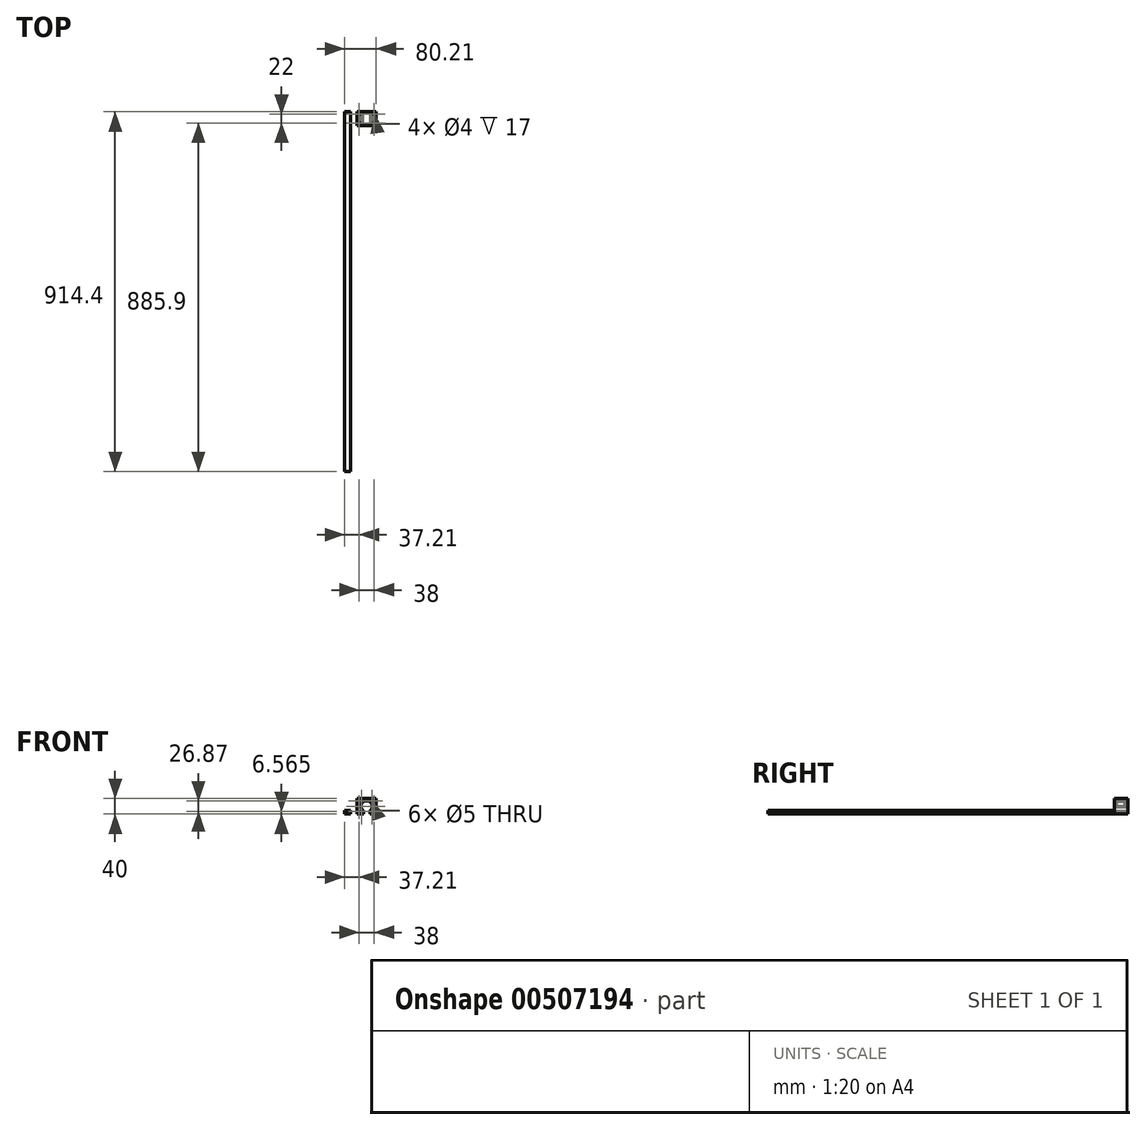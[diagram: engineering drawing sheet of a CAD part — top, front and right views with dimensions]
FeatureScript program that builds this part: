
annotation { "Feature Type Name" : "Feature", "Feature Type Description" : "" }
export const myFeature = defineFeature(function(context is Context, id is Id, definition is map)
    precondition{}
    {
        {
            var Q0;
            Q0=qCreatedBy(makeId("Front.planeOp"),FACE);
            var sketch = newSketch(context, id + "F0", { "sketchPlane" : qUnion([Q0])});
            skLineSegment(sketch, "E0.bottom", {"start": v(0, 0) * mm, "end": v(48, 0) * mm});
            skLineSegment(sketch, "E0.top", {"start": v(0, 40) * mm, "end": v(48, 40) * mm});
            skLineSegment(sketch, "E0.left", {"start": v(0, 0) * mm, "end": v(0, 40) * mm});
            skLineSegment(sketch, "E0.right", {"start": v(48, 0) * mm, "end": v(48, 40) * mm});
            skLineSegment(sketch, "E1", {"start": v(24, 40) * mm, "end": v(24, 0) * mm, "construction": true});
            skCircle(sketch, "E2", {"center": v(24, 20) * mm, "radius": 14.05 * mm});
            skLineSegment(sketch, "E3", {"start": v(32.5, 0) * mm, "end": v(32.5, 8.81) * mm});
            skCircle(sketch, "E4", {"center": v(24, 20) * mm, "radius": 19 * mm, "construction": true});
            skCircle(sketch, "E5", {"center": v(37.44, 6.56) * mm, "radius": 2.5 * mm});
            skLineSegment(sketch, "E6", {"start": v(0, 20) * mm, "end": v(48, 20) * mm, "construction": true});
            skLineSegment(sketch, "E7", {"start": v(24, 20) * mm, "end": v(37.44, 6.56) * mm, "construction": true});
            skCircle(sketch, "E8.1.0", {"center": v(43, 20) * mm, "radius": 2.5 * mm});
            skCircle(sketch, "E8.2.0", {"center": v(37.44, 33.44) * mm, "radius": 2.5 * mm});
            skLineSegment(sketch, "E8.anchor2", {"start": v(24, 20) * mm, "end": v(37.44, 33.44) * mm, "construction": true});
            skLineSegment(sketch, "E9.MirrorCS", {"start": v(15.5, 0) * mm, "end": v(15.5, 8.81) * mm});
            skCircle(sketch, "E10.MirrorC", {"center": v(10.56, 6.56) * mm, "radius": 2.5 * mm});
            skCircle(sketch, "E11.MirrorC", {"center": v(5, 20) * mm, "radius": 2.5 * mm});
            skCircle(sketch, "E12.MirrorC", {"center": v(10.56, 33.44) * mm, "radius": 2.5 * mm});
            skSolve(sketch);
        }
        {
            var Q0;
            Q0=makeQuery(id+"F0.imprint","IMPRINT",FACE,{"disambiguationData":[TD([[makeQuery(id+"F0.imprint","IMPRINT",EDGE,{"derivedFrom":sQuery(id+"F0.wireOp",EDGE,"E0.top")}),-1.0]])]});
            extrude(context, id + "F1", {"entities" : qUnion([Q0]), "depth" : 35 * mm});
        }
        {
            var Q0;
            Q0=makeQuery(id+"F1.opExtrude","SWEPT_FACE",FACE,{"disambiguationData":[OSD([sQuery(id+"F0.wireOp",EDGE,"E0.top")])]});
            var sketch = newSketch(context, id + "F2", { "sketchPlane" : qUnion([Q0])});
            skCircle(sketch, "E13.MirrorC", {"center": v(43, -6.5) * mm, "radius": 2 * mm});
            skCircle(sketch, "E14.0.1.0", {"center": v(43, -28.5) * mm, "radius": 2 * mm});
            skCircle(sketch, "E14.1.0.0", {"center": v(5, -6.5) * mm, "radius": 2 * mm});
            skCircle(sketch, "E14.1.1.0", {"center": v(5, -28.5) * mm, "radius": 2 * mm});
            skLineSegment(sketch, "E14.direction1", {"start": v(43, -6.5) * mm, "end": v(5, -6.5) * mm, "construction": true});
            skLineSegment(sketch, "E14.direction2", {"start": v(43, -6.5) * mm, "end": v(43, -28.5) * mm, "construction": true});
            skSolve(sketch);
        }
        {
            var Q0;
            Q0 = qSketchRegion(id + "F2", true);
            extrude(context, id + "F3", {"entities" : qUnion([Q0]), "operationType" : NewBodyOperationType.REMOVE, "oppositeDirection" : true, "depth" : 17 * mm});
        }
        {
            var Q0;
            Q0=qCreatedBy(makeId("Front.planeOp"),FACE);
            var sketch = newSketch(context, id + "F4", { "sketchPlane" : qUnion([Q0])});
            skLineSegment(sketch, "E15.bottom", {"start": v(-32.2, 0) * mm, "end": v(-17.2, 0) * mm});
            skLineSegment(sketch, "E15.top", {"start": v(-32.2, 10) * mm, "end": v(-17.2, 10) * mm});
            skLineSegment(sketch, "E15.left", {"start": v(-32.2, 0) * mm, "end": v(-32.2, 10) * mm});
            skLineSegment(sketch, "E15.right", {"start": v(-17.2, 0) * mm, "end": v(-17.2, 10) * mm});
            skLineSegment(sketch, "E16.1.0.0", {"start": v(-42.6, 0) * mm, "end": v(-42.6, 10) * mm});
            skLineSegment(sketch, "E16.1.0.1", {"start": v(-57.6, 10) * mm, "end": v(-42.6, 10) * mm});
            skLineSegment(sketch, "E16.1.0.2", {"start": v(-57.6, 0) * mm, "end": v(-42.6, 0) * mm});
            skLineSegment(sketch, "E16.1.0.3", {"start": v(-57.6, 0) * mm, "end": v(-57.6, 10) * mm});
            skLineSegment(sketch, "E16.2.0.0", {"start": v(-68, 0) * mm, "end": v(-68, 10) * mm});
            skLineSegment(sketch, "E16.2.0.1", {"start": v(-83, 10) * mm, "end": v(-68, 10) * mm});
            skLineSegment(sketch, "E16.2.0.2", {"start": v(-83, 0) * mm, "end": v(-68, 0) * mm});
            skLineSegment(sketch, "E16.2.0.3", {"start": v(-83, 0) * mm, "end": v(-83, 10) * mm});
            skLineSegment(sketch, "E16.direction1", {"start": v(-32.2, 0) * mm, "end": v(-57.6, 0) * mm, "construction": true});
            skSolve(sketch);
        }
        {
            var Q0;
            Q0=makeQuery(id+"F4.imprint","IMPRINT",FACE,{"disambiguationData":[TD([[makeQuery(id+"F4.imprint","IMPRINT",EDGE,{"derivedFrom":sQuery(id+"F4.wireOp",EDGE,"E15.bottom")}),1.0]])]});
            extrude(context, id + "F5", {"entities" : qUnion([Q0]), "depth" : 914.4 * mm});
        }
    });
